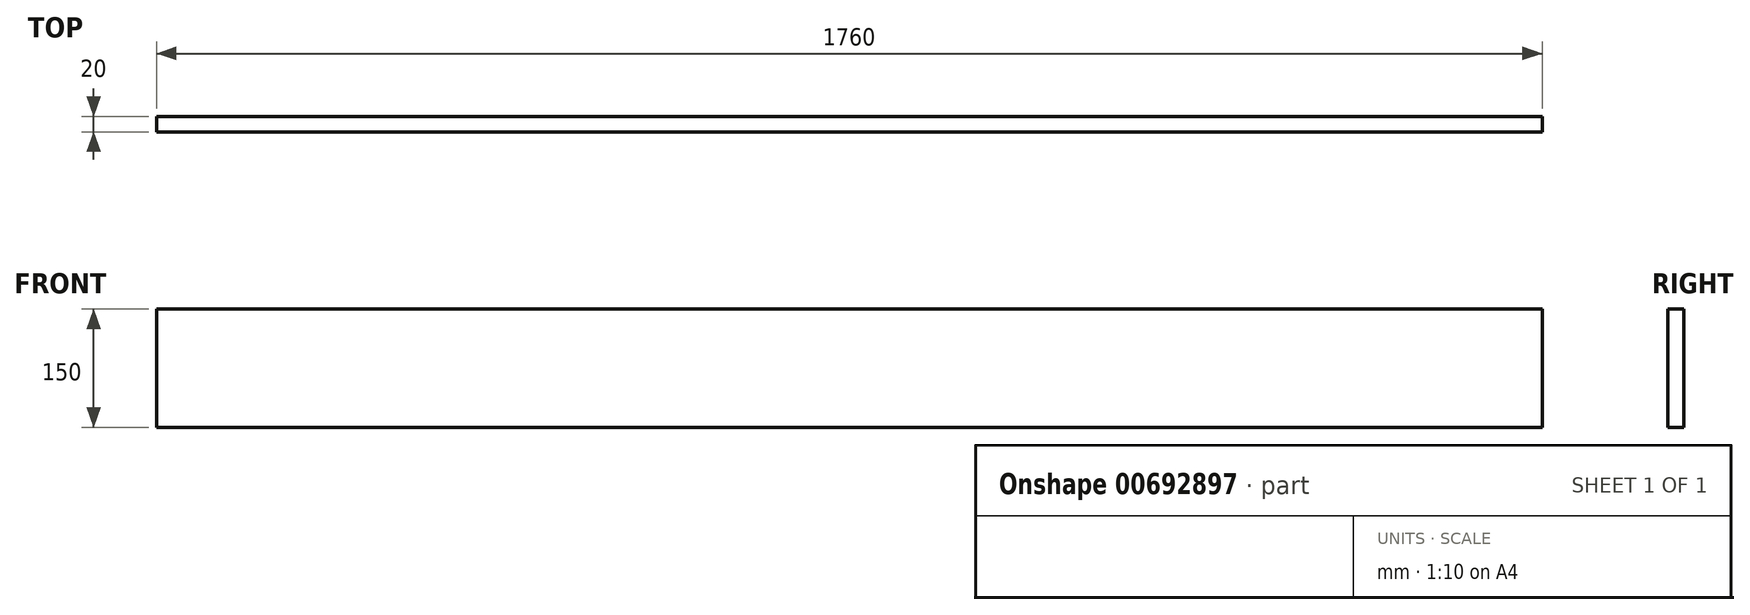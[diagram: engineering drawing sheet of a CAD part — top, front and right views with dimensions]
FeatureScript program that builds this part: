
annotation { "Feature Type Name" : "Feature", "Feature Type Description" : "" }
export const myFeature = defineFeature(function(context is Context, id is Id, definition is map)
    precondition{}
    {
        {
            var Q0;
            Q0=qCreatedBy(makeId("Front.planeOp"),FACE);
            var sketch = newSketch(context, id + "F0", { "sketchPlane" : qUnion([Q0])});
            skLineSegment(sketch, "E0.bottom", {"start": v(0, 150) * mm, "end": v(1760, 150) * mm});
            skLineSegment(sketch, "E0.top", {"start": v(0, 0) * mm, "end": v(1760, 0) * mm});
            skLineSegment(sketch, "E0.left", {"start": v(0, 150) * mm, "end": v(0, 0) * mm});
            skLineSegment(sketch, "E0.right", {"start": v(1760, 150) * mm, "end": v(1760, 0) * mm});
            skSolve(sketch);
        }
        {
            var Q0;
            Q0=makeQuery(id+"F0.imprint","IMPRINT",FACE,{"disambiguationData":[TD([[makeQuery(id+"F0.imprint","IMPRINT",EDGE,{"derivedFrom":sQuery(id+"F0.wireOp",EDGE,"E0.bottom")}),-1.0]])]});
            extrude(context, id + "F1", {"entities" : qUnion([Q0]), "depth" : 20 * mm, "offsetDistance" : 25 * mm});
        }
    });
